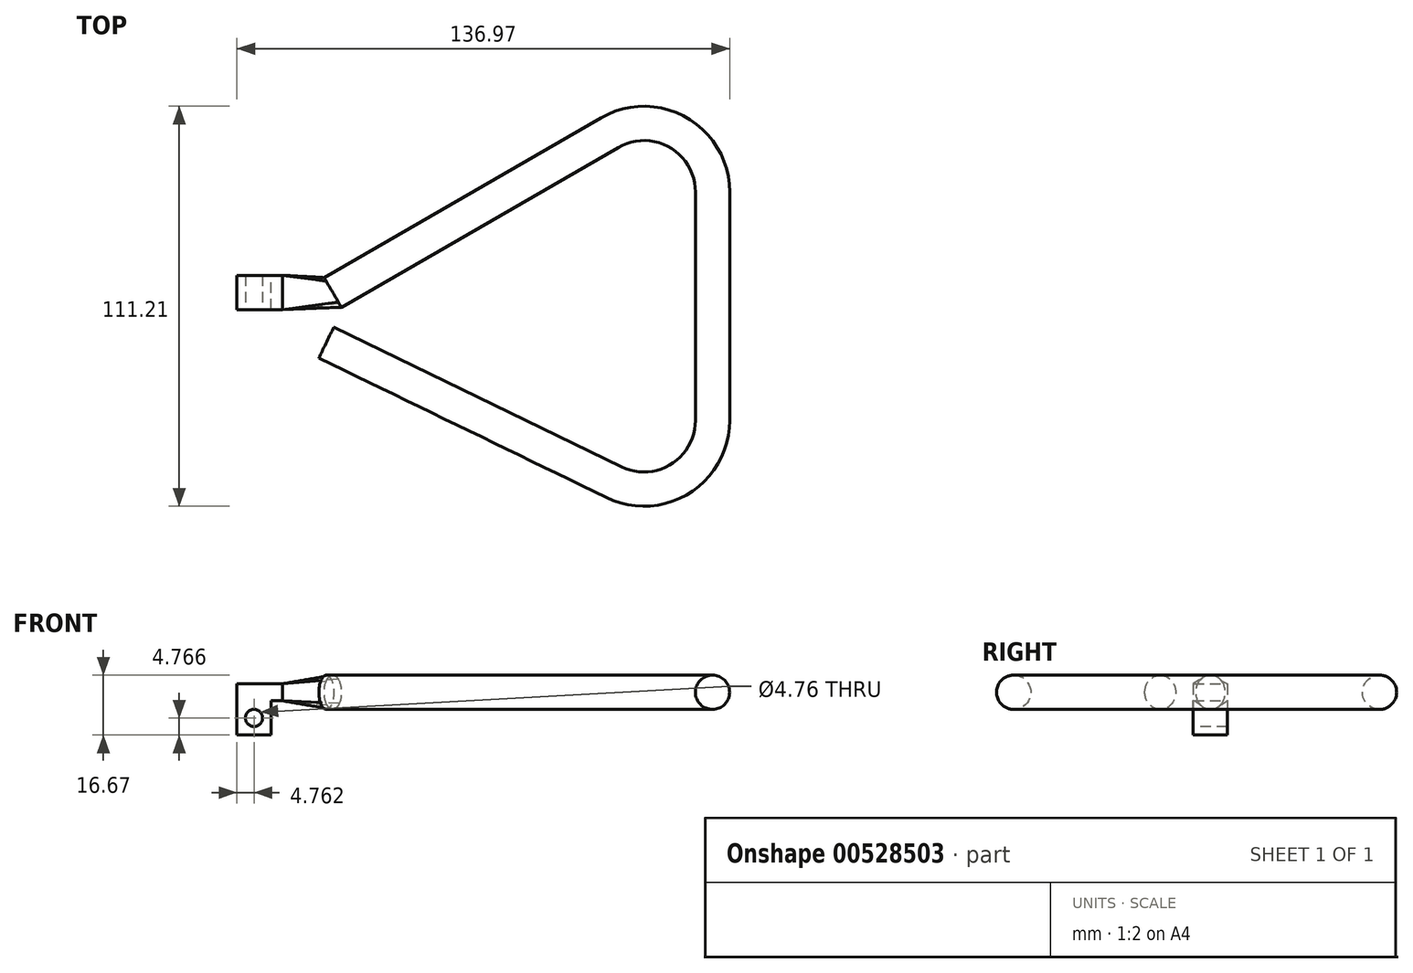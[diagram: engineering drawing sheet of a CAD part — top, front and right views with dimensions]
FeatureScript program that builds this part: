
annotation { "Feature Type Name" : "Feature", "Feature Type Description" : "" }
export const myFeature = defineFeature(function(context is Context, id is Id, definition is map)
    precondition{}
    {
        {
            var Q0;
            Q0=qCreatedBy(makeId("Top.planeOp"),FACE);
            var sketch = newSketch(context, id + "F0", { "sketchPlane" : qUnion([Q0])});
            skLineSegment(sketch, "E0", {"start": v(12.16, -5.9) * mm, "end": v(92.14, -44.72) * mm});
            skLineSegment(sketch, "E1", {"start": v(119.51, -27.58) * mm, "end": v(119.51, 36) * mm});
            skLineSegment(sketch, "E2", {"start": v(90.94, 52.5) * mm, "end": v(13.95, 8.05) * mm});
            skPoint(sketch, "E3.visualSharp", {"position": v(119.51, 69) * mm});
            skArc(sketch, "E3.filletArc", {"start": v(119.51, 36) * mm, "mid": v(109.99, 52.5) * mm, "end": v(90.94, 52.5) * mm});
            skPoint(sketch, "E4.visualSharp", {"position": v(119.51, -58) * mm});
            skArc(sketch, "E4.filletArc", {"start": v(92.14, -44.72) * mm, "mid": v(110.57, -43.73) * mm, "end": v(119.51, -27.58) * mm});
            skPoint(sketch, "E5", {"position": v(12.16, -5.9) * mm});
            skLineSegment(sketch, "E6", {"start": v(10.78, -8.76) * mm, "end": v(13.55, -3.05) * mm});
            skLineSegment(sketch, "E7", {"start": v(12.36, 10.8) * mm, "end": v(15.53, 5.3) * mm});
            skSolve(sketch);
        }
        {
            var Q0;
            Q0=sQuery(id+"F0.wireOp",EDGE,"E6");
            var Q1;
            Q1=sQuery(id+"F0.wireOp",EDGE,"E0");
            cPlane(context, id + "F1", {"entities" : qUnion([Q0, Q1]), "cplaneType" : CPlaneType.LINE_ANGLE, "offset" : 25.4 * mm, "angle" : 90 * degree, "width" : 152.4 * mm, "height" : 152.4 * mm});
        }
        {
            var Q0;
            Q0=qCreatedBy(id+"F1.planeOp",FACE);
            var sketch = newSketch(context, id + "F2", { "sketchPlane" : qUnion([Q0])});
            skCircle(sketch, "E8", {"center": v(0, 0) * mm, "radius": 4.76 * mm});
            skSolve(sketch);
        }
        {
            var Q0;
            Q0=makeQuery(id+"F2.imprint","IMPRINT",FACE,{"disambiguationData":[TD([[makeQuery(id+"F2.imprint","IMPRINT",EDGE,{"derivedFrom":sQuery(id+"F2.wireOp",EDGE,"E8")}),1.0]])]});
            var Q1;
            Q1=sQuery(id+"F0.wireOp",EDGE,"E0");
            var Q2;
            Q2=sQuery(id+"F0.wireOp",EDGE,"E4.filletArc");
            var Q3;
            Q3=sQuery(id+"F0.wireOp",EDGE,"E1");
            var Q4;
            Q4=sQuery(id+"F0.wireOp",EDGE,"E3.filletArc");
            var Q5;
            Q5=sQuery(id+"F0.wireOp",EDGE,"E2");
            sweep(context, id + "F3", {"profiles" : qUnion([Q0]), "path" : qUnion([Q1, Q2, Q3, Q4, Q5])});
        }
        {
            var Q0;
            Q0=qCreatedBy(makeId("Right.planeOp"),FACE);
            var sketch = newSketch(context, id + "F4", { "sketchPlane" : qUnion([Q0])});
            skLineSegment(sketch, "E9.bottom", {"start": v(3.29, 2.38) * mm, "end": v(12.81, 2.38) * mm});
            skLineSegment(sketch, "E9.top", {"start": v(3.29, -2.38) * mm, "end": v(12.81, -2.38) * mm});
            skLineSegment(sketch, "E9.left", {"start": v(3.29, 2.38) * mm, "end": v(3.29, -2.38) * mm});
            skLineSegment(sketch, "E9.right", {"start": v(12.81, 2.38) * mm, "end": v(12.81, -2.38) * mm});
            skPoint(sketch, "E9.middle", {"position": v(8.05, 0) * mm});
            skLineSegment(sketch, "E10", {"start": v(8.05, 15.41) * mm, "end": v(8.05, -15.41) * mm, "construction": true});
            skSolve(sketch);
        }
        {
            var Q1;
            Q1=makeQuery(id+"F3.opSweep","CAP_FACE",FACE,{"disambiguationData":[OSD([sQuery(id+"F0.wireOp",VERTEX,"E2.end"),sQuery(id+"F2.wireOp",EDGE,"E8")])],"isStart":false});
            var Q2;
            Q2=qSketchRegion(id+"F4",true);
            loft(context, id + "F5", {"operationType" : NewBodyOperationType.ADD, "sheetProfilesArray" : [{ "sheetProfileEntities" : qUnion([Q1]) }, { "sheetProfileEntities" : qUnion([Q2]) }]});
        }
        {
            var Q0;
            Q0=makeQuery(id+"F5.opLoft","CAP_FACE",FACE,{"disambiguationData":[OSD([makeQuery(id+"F4.imprint","IMPRINT",FACE,{"disambiguationData":[TD([[makeQuery(id+"F4.imprint","IMPRINT",EDGE,{"derivedFrom":sQuery(id+"F4.wireOp",EDGE,"E9.bottom")}),-1.0]])]})])],"isStart":true});
            var sketch = newSketch(context, id + "F6", { "sketchPlane" : qUnion([Q0])});
            skLineSegment(sketch, "E11.0", {"start": v(-3.29, 2.38) * mm, "end": v(-12.81, 2.38) * mm});
            skLineSegment(sketch, "E11.1", {"start": v(-3.29, -2.38) * mm, "end": v(-3.29, 2.38) * mm});
            skLineSegment(sketch, "E11.2", {"start": v(-12.81, -2.38) * mm, "end": v(-3.29, -2.38) * mm});
            skLineSegment(sketch, "E11.3", {"start": v(-12.81, 2.38) * mm, "end": v(-12.81, -2.38) * mm});
            skSolve(sketch);
        }
        {
            var Q0;
            Q0=qSketchRegion(id+"F6",true);
            extrude(context, id + "F7", {"entities" : qUnion([Q0]), "operationType" : NewBodyOperationType.ADD, "depth" : 12.7 * mm, "offsetDistance" : 25.4 * mm});
        }
        {
            var Q0;
            Q0=makeQuery(id+"F7.opExtrude","SWEPT_FACE",FACE,{"disambiguationData":[OSD([sQuery(id+"F6.wireOp",EDGE,"E11.2")])]});
            var sketch = newSketch(context, id + "F8", { "sketchPlane" : qUnion([Q0])});
            skPoint(sketch, "E12.0", {"position": v(-12.7, -3.29) * mm});
            skPoint(sketch, "E13.0", {"position": v(-12.7, -12.81) * mm});
            skLineSegment(sketch, "E14.bottom", {"start": v(-12.7, -3.29) * mm, "end": v(-3.18, -3.29) * mm});
            skLineSegment(sketch, "E14.top", {"start": v(-12.7, -12.81) * mm, "end": v(-3.18, -12.81) * mm});
            skLineSegment(sketch, "E14.left", {"start": v(-12.7, -3.29) * mm, "end": v(-12.7, -12.81) * mm});
            skLineSegment(sketch, "E14.right", {"start": v(-3.18, -3.29) * mm, "end": v(-3.17, -12.81) * mm});
            skSolve(sketch);
        }
        {
            var Q0;
            Q0=makeQuery(id+"F8.imprint","IMPRINT",FACE,{"disambiguationData":[TD([[makeQuery(id+"F8.imprint","IMPRINT",EDGE,{"derivedFrom":sQuery(id+"F8.wireOp",EDGE,"E14.bottom")}),1.0]])]});
            extrude(context, id + "F9", {"entities" : qUnion([Q0]), "operationType" : NewBodyOperationType.ADD, "depth" : 9.52 * mm, "offsetDistance" : 25.4 * mm});
        }
        {
            var Q0;
            Q0=makeQuery(id+"F9.boolean.opBoolean","MERGE",FACE,{"derivedFrom":[makeQuery(id+"F7.opExtrude","SWEPT_FACE",FACE,{"disambiguationData":[OSD([sQuery(id+"F6.wireOp",EDGE,"E11.1")])]}),makeQuery(id+"F9.opExtrude","SWEPT_FACE",FACE,{"disambiguationData":[OSD([sQuery(id+"F8.wireOp",EDGE,"E14.bottom")])]})]});
            var sketch = newSketch(context, id + "F10", { "sketchPlane" : qUnion([Q0])});
            skPoint(sketch, "E15.0", {"position": v(-7.94, -11.9) * mm});
            skLineSegment(sketch, "E16", {"start": v(-7.94, -11.9) * mm, "end": v(-7.94, 2.38) * mm, "construction": true});
            skPoint(sketch, "E17.0", {"position": v(-3.18, -7.14) * mm});
            skLineSegment(sketch, "E18", {"start": v(-3.18, -7.14) * mm, "end": v(-12.7, -7.14) * mm, "construction": true});
            skPoint(sketch, "E19", {"position": v(-7.94, -7.14) * mm});
            skCircle(sketch, "E20", {"center": v(-7.94, -7.14) * mm, "radius": 2.38 * mm});
            skSolve(sketch);
        }
        {
            var Q0;
            Q0=makeQuery(id+"F10.imprint","IMPRINT",FACE,{"disambiguationData":[TD([[makeQuery(id+"F10.imprint","IMPRINT",EDGE,{"derivedFrom":sQuery(id+"F10.wireOp",EDGE,"E20")}),1.0]])]});
            extrude(context, id + "F11", {"entities" : qUnion([Q0]), "operationType" : NewBodyOperationType.REMOVE, "endBound" : BoundingType.THROUGH_ALL, "oppositeDirection" : true, "depth" : 25.4 * mm, "offsetDistance" : 25.4 * mm});
        }
    });
